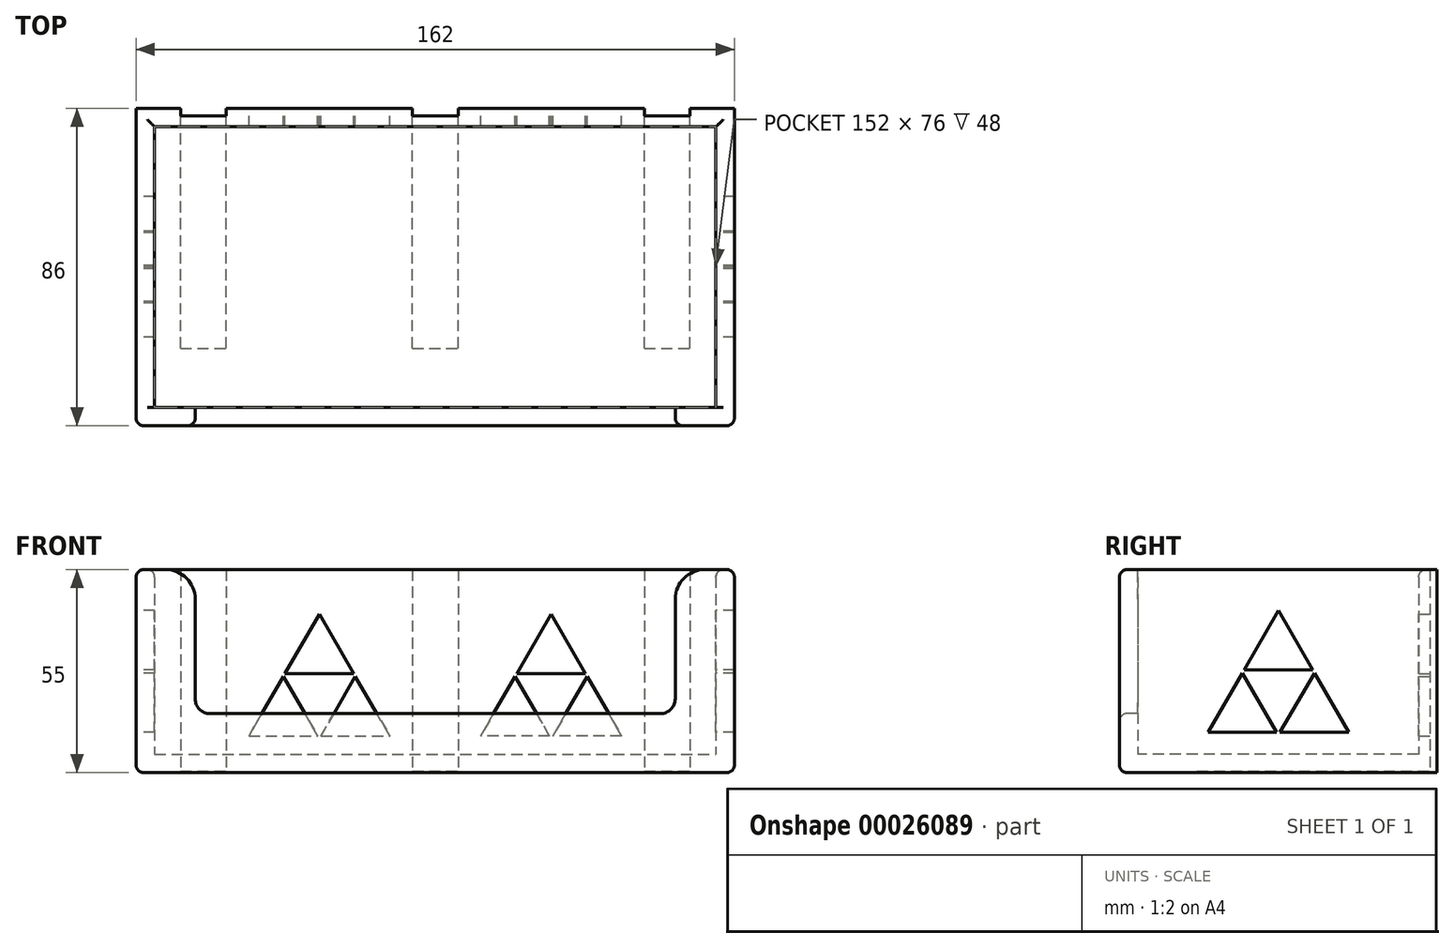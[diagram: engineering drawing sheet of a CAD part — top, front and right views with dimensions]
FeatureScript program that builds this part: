
annotation { "Feature Type Name" : "Feature", "Feature Type Description" : "" }
export const myFeature = defineFeature(function(context is Context, id is Id, definition is map)
    precondition{}
    {
        {
            var Q0;
            Q0=qCreatedBy(makeId("Top.planeOp"),FACE);
            var sketch = newSketch(context, id + "F0", { "sketchPlane" : qUnion([Q0])});
            skLineSegment(sketch, "E0.bottom", {"start": v(-78.63, 86.65) * mm, "end": v(73.37, 86.65) * mm});
            skLineSegment(sketch, "E0.top", {"start": v(-78.63, 10.65) * mm, "end": v(73.37, 10.65) * mm});
            skLineSegment(sketch, "E0.left", {"start": v(-78.63, 86.65) * mm, "end": v(-78.63, 10.65) * mm});
            skLineSegment(sketch, "E0.right", {"start": v(73.37, 86.65) * mm, "end": v(73.37, 10.65) * mm});
            skSolve(sketch);
        }
        {
            var Q0;
            Q0=makeQuery(id+"F0.imprint","IMPRINT",FACE,{"disambiguationData":[TD([[makeQuery(id+"F0.imprint","IMPRINT",EDGE,{"derivedFrom":sQuery(id+"F0.wireOp",EDGE,"E0.bottom")}),-1.0]])]});
            extrude(context, id + "F1", {"entities" : qUnion([Q0]), "depth" : 5 * mm});
        }
        {
            var Q0;
            Q0=qCreatedBy(makeId("Top.planeOp"),FACE);
            var sketch = newSketch(context, id + "F2", { "sketchPlane" : qUnion([Q0])});
            skLineSegment(sketch, "E1.0", {"start": v(-78.63, 10.65) * mm, "end": v(73.37, 10.65) * mm});
            skLineSegment(sketch, "E2.0", {"start": v(-78.63, 86.65) * mm, "end": v(-78.63, 10.65) * mm});
            skLineSegment(sketch, "E3.0", {"start": v(-78.63, 86.65) * mm, "end": v(73.37, 86.65) * mm});
            skLineSegment(sketch, "E4.0", {"start": v(73.37, 86.65) * mm, "end": v(73.37, 10.65) * mm});
            skLineSegment(sketch, "E5.0", {"start": v(-83.63, 5.65) * mm, "end": v(78.37, 5.65) * mm});
            skLineSegment(sketch, "E6.0", {"start": v(-83.63, 91.65) * mm, "end": v(78.37, 91.65) * mm});
            skLineSegment(sketch, "E7.0", {"start": v(-83.63, 91.65) * mm, "end": v(-83.63, 5.65) * mm});
            skLineSegment(sketch, "E8.0", {"start": v(78.37, 91.65) * mm, "end": v(78.37, 5.65) * mm});
            skSolve(sketch);
        }
        {
            var Q0;
            Q0=makeQuery(id+"F2.imprint","IMPRINT",FACE,{"disambiguationData":[TD([[makeQuery(id+"F2.imprint","IMPRINT",EDGE,{"derivedFrom":sQuery(id+"F2.wireOp",EDGE,"E1.0")}),-1.0]])]});
            extrude(context, id + "F3", {"entities" : qUnion([Q0]), "operationType" : NewBodyOperationType.ADD, "depth" : 55 * mm});
        }
        {
            var Q0;
            Q0=makeQuery(id+"F3.opExtrude","SWEPT_FACE",FACE,{"disambiguationData":[OSD([sQuery(id+"F2.wireOp",EDGE,"E5.0")])]});
            var sketch = newSketch(context, id + "F4", { "sketchPlane" : qUnion([Q0])});
            skLineSegment(sketch, "E9.0", {"start": v(-63.63, 16) * mm, "end": v(58.37, 16) * mm});
            skLineSegment(sketch, "E10.0", {"start": v(-67.63, 47) * mm, "end": v(-67.63, 20) * mm});
            skLineSegment(sketch, "E11.0", {"start": v(62.37, 47) * mm, "end": v(62.37, 20) * mm});
            skLineSegment(sketch, "E12.0", {"start": v(-83.63, 55) * mm, "end": v(-75.63, 55) * mm});
            skLineSegment(sketch, "E13.trimOffspring", {"start": v(70.37, 55) * mm, "end": v(78.37, 55) * mm});
            skPoint(sketch, "E14.visualSharp", {"position": v(-67.63, 55) * mm});
            skArc(sketch, "E14.filletArc", {"start": v(-67.63, 47) * mm, "mid": v(-69.98, 52.66) * mm, "end": v(-75.63, 55) * mm});
            skPoint(sketch, "E15.visualSharp", {"position": v(62.37, 55) * mm});
            skArc(sketch, "E15.filletArc", {"start": v(70.37, 55) * mm, "mid": v(64.7, 52.66) * mm, "end": v(62.37, 47) * mm});
            skPoint(sketch, "E16.visualSharp", {"position": v(-67.63, 16) * mm});
            skArc(sketch, "E16.filletArc", {"start": v(-67.63, 20) * mm, "mid": v(-66.46, 17.17) * mm, "end": v(-63.63, 16) * mm});
            skPoint(sketch, "E17.visualSharp", {"position": v(62.37, 16) * mm});
            skArc(sketch, "E17.filletArc", {"start": v(58.37, 16) * mm, "mid": v(61.2, 17.17) * mm, "end": v(62.37, 20) * mm});
            skSolve(sketch);
        }
        {
            var Q0;
            Q0=makeQuery(id+"F4.imprint","IMPRINT",FACE,{"disambiguationData":[TD([[makeQuery(id+"F4.imprint","IMPRINT",EDGE,{"derivedFrom":sQuery(id+"F4.wireOp",EDGE,"E9.0")}),1.0]])]});
            var Q1;
            Q1=makeQuery(id+"F3.opExtrude","SWEPT_FACE",FACE,{"disambiguationData":[OSD([sQuery(id+"F2.wireOp",EDGE,"E1.0")])]});
            extrude(context, id + "F5", {"entities" : qUnion([Q0]), "operationType" : NewBodyOperationType.REMOVE, "endBound" : BoundingType.UP_TO_SURFACE, "oppositeDirection" : true, "endBoundEntityFace" : qUnion([Q1]), "depth" : 25.4 * mm});
        }
        {
            var Q0;
            Q0=makeQuery(id+"F3.opExtrude","SWEPT_FACE",FACE,{"disambiguationData":[OSD([sQuery(id+"F2.wireOp",EDGE,"E6.0")])]});
            var sketch = newSketch(context, id + "F6", { "sketchPlane" : qUnion([Q0])});
            skLineSegment(sketch, "E18.0", {"start": v(-78.37, 55) * mm, "end": v(-78.37, 0) * mm});
            skLineSegment(sketch, "E19.0", {"start": v(83.63, 0) * mm, "end": v(-78.37, 0) * mm});
            skLineSegment(sketch, "E20.0", {"start": v(83.63, 55) * mm, "end": v(83.63, 0) * mm});
            skLineSegment(sketch, "E21.0", {"start": v(83.63, 55) * mm, "end": v(-78.37, 55) * mm});
            skLineSegment(sketch, "E22", {"start": v(2.63, 55) * mm, "end": v(2.63, 0) * mm, "construction": true});
            skLineSegment(sketch, "E23.0", {"start": v(-3.57, 70) * mm, "end": v(-3.57, 0) * mm});
            skLineSegment(sketch, "E24.0", {"start": v(8.83, 70) * mm, "end": v(8.83, 0) * mm});
            skLineSegment(sketch, "E25.0", {"start": v(-66.37, 70) * mm, "end": v(-66.37, 0) * mm});
            skLineSegment(sketch, "E26.0", {"start": v(-53.97, 70) * mm, "end": v(-53.97, 0) * mm});
            skLineSegment(sketch, "E27.0", {"start": v(71.63, 70) * mm, "end": v(71.63, 0) * mm});
            skLineSegment(sketch, "E28.0", {"start": v(59.23, 70) * mm, "end": v(59.23, 0) * mm});
            skSolve(sketch);
        }
        {
            var Q0;
            {var subQ0=sQuery(id+"F6.wireOp",EDGE,"E25.0");Q0=makeQuery(id+"F6.imprint","IMPRINT",FACE,{"disambiguationData":[TD([[makeQuery(id+"F6.imprint","IMPRINT",EDGE,{"derivedFrom":subQ0}),1.0]])]});}
            var Q1;
            {var subQ0=sQuery(id+"F6.wireOp",EDGE,"E23.0");Q1=makeQuery(id+"F6.imprint","IMPRINT",FACE,{"disambiguationData":[TD([[makeQuery(id+"F6.imprint","IMPRINT",EDGE,{"derivedFrom":subQ0}),1.0]])]});}
            var Q2;
            {var subQ0=sQuery(id+"F6.wireOp",EDGE,"E27.0");Q2=makeQuery(id+"F6.imprint","IMPRINT",FACE,{"disambiguationData":[TD([[makeQuery(id+"F6.imprint","IMPRINT",EDGE,{"derivedFrom":subQ0}),-1.0]])]});}
            extrude(context, id + "F7", {"entities" : qUnion([Q0, Q1, Q2]), "operationType" : NewBodyOperationType.REMOVE, "oppositeDirection" : true, "depth" : 2 * mm});
        }
        {
            var Q0;
            Q0=makeQuery(id+"F3.boolean.opBoolean","MERGE",FACE,{"derivedFrom":[makeQuery(id+"F1.opExtrude","CAP_FACE",FACE,{"disambiguationData":[OSD([sQuery(id+"F0.wireOp",EDGE,"E0.bottom"),sQuery(id+"F0.wireOp",EDGE,"E0.top"),sQuery(id+"F0.wireOp",EDGE,"E0.left"),sQuery(id+"F0.wireOp",EDGE,"E0.right")])],"isStart":true}),makeQuery(id+"F3.opExtrude","CAP_FACE",FACE,{"disambiguationData":[OSD([sQuery(id+"F2.wireOp",EDGE,"E1.0"),sQuery(id+"F2.wireOp",EDGE,"E2.0"),sQuery(id+"F2.wireOp",EDGE,"E3.0"),sQuery(id+"F2.wireOp",EDGE,"E4.0"),sQuery(id+"F2.wireOp",EDGE,"E5.0"),sQuery(id+"F2.wireOp",EDGE,"E6.0"),sQuery(id+"F2.wireOp",EDGE,"E7.0"),sQuery(id+"F2.wireOp",EDGE,"E8.0")])],"isStart":true})]});
            var sketch = newSketch(context, id + "F8", { "sketchPlane" : qUnion([Q0])});
            skLineSegment(sketch, "E29.0", {"start": v(66.37, -91.65) * mm, "end": v(78.37, -91.65) * mm, "construction": true});
            skLineSegment(sketch, "E30.0", {"start": v(78.37, -91.65) * mm, "end": v(78.37, -5.65) * mm, "construction": true});
            skLineSegment(sketch, "E31.0", {"start": v(53.97, -89.65) * mm, "end": v(66.37, -89.65) * mm});
            skLineSegment(sketch, "E32.0", {"start": v(66.37, -26.65) * mm, "end": v(66.37, -91.65) * mm});
            skLineSegment(sketch, "E33.0", {"start": v(53.97, -26.65) * mm, "end": v(53.97, -91.65) * mm});
            skLineSegment(sketch, "E34.0", {"start": v(3.57, -91.65) * mm, "end": v(53.97, -91.65) * mm, "construction": true});
            skLineSegment(sketch, "E35.0", {"start": v(3.57, -26.65) * mm, "end": v(3.57, -91.65) * mm});
            skLineSegment(sketch, "E36.0", {"start": v(-8.83, -89.65) * mm, "end": v(3.57, -89.65) * mm});
            skLineSegment(sketch, "E37.0", {"start": v(-8.83, -26.65) * mm, "end": v(-8.83, -91.65) * mm});
            skLineSegment(sketch, "E38.0", {"start": v(-59.23, -91.65) * mm, "end": v(-8.83, -91.65) * mm, "construction": true});
            skLineSegment(sketch, "E39.0", {"start": v(-59.23, -26.65) * mm, "end": v(-59.23, -91.65) * mm});
            skLineSegment(sketch, "E40.0", {"start": v(-71.63, -89.65) * mm, "end": v(-59.23, -89.65) * mm});
            skLineSegment(sketch, "E41.0", {"start": v(-71.63, -26.65) * mm, "end": v(-71.63, -91.65) * mm});
            skLineSegment(sketch, "E42.0", {"start": v(-83.63, -91.65) * mm, "end": v(-71.63, -91.65) * mm, "construction": true});
            skLineSegment(sketch, "E43.0", {"start": v(-83.63, -91.65) * mm, "end": v(-83.63, -5.65) * mm, "construction": true});
            skLineSegment(sketch, "E44.0", {"start": v(-71.63, -26.65) * mm, "end": v(-59.23, -26.65) * mm});
            skLineSegment(sketch, "E45.trimOffspring", {"start": v(53.97, -26.65) * mm, "end": v(66.37, -26.65) * mm});
            skLineSegment(sketch, "E46.trimOffspring", {"start": v(-8.83, -26.65) * mm, "end": v(3.57, -26.65) * mm});
            skSolve(sketch);
        }
        {
            var Q0;
            {var subQ0=sQuery(id+"F8.wireOp",EDGE,"E36.0");Q0=makeQuery(id+"F8.imprint","IMPRINT",FACE,{"disambiguationData":[TD([[makeQuery(id+"F8.imprint","IMPRINT",EDGE,{"derivedFrom":subQ0}),1.0]])]});}
            var Q1;
            {var subQ0=sQuery(id+"F8.wireOp",EDGE,"E40.0");Q1=makeQuery(id+"F8.imprint","IMPRINT",FACE,{"disambiguationData":[TD([[makeQuery(id+"F8.imprint","IMPRINT",EDGE,{"derivedFrom":subQ0}),1.0]])]});}
            var Q2;
            {var subQ0=sQuery(id+"F8.wireOp",EDGE,"E31.0");Q2=makeQuery(id+"F8.imprint","IMPRINT",FACE,{"disambiguationData":[TD([[makeQuery(id+"F8.imprint","IMPRINT",EDGE,{"derivedFrom":subQ0}),1.0]])]});}
            extrude(context, id + "F9", {"entities" : qUnion([Q0, Q1, Q2]), "operationType" : NewBodyOperationType.REMOVE, "oppositeDirection" : true, "depth" : .4 * mm});
        }
        {
            var Q0;
            Q0=makeQuery(id+"F3.opExtrude","SWEPT_FACE",FACE,{"disambiguationData":[OSD([sQuery(id+"F2.wireOp",EDGE,"E7.0")])]});
            var sketch = newSketch(context, id + "F10", { "sketchPlane" : qUnion([Q0])});
            skLineSegment(sketch, "E47.0", {"start": v(-91.65, 55) * mm, "end": v(-5.65, 55) * mm});
            skLineSegment(sketch, "E48.0", {"start": v(-91.65, 55) * mm, "end": v(-91.65, 0) * mm});
            skLineSegment(sketch, "E49.0", {"start": v(-91.65, 0) * mm, "end": v(-5.65, 0) * mm});
            skLineSegment(sketch, "E50.0", {"start": v(-5.65, 55) * mm, "end": v(-5.65, 0) * mm});
            skLineSegment(sketch, "E51.2", {"start": v(-67.7, 10.9) * mm, "end": v(-49.11, 10.9) * mm});
            skLineSegment(sketch, "E52", {"start": v(-48.65, 43.9) * mm, "end": v(-57.95, 27.8) * mm});
            skLineSegment(sketch, "E53", {"start": v(-48.65, 43.9) * mm, "end": v(-39.36, 27.8) * mm});
            skPoint(sketch, "E51.1.start.orphan", {"position": v(-80.85, 43.9) * mm});
            skPoint(sketch, "E54.orphan", {"position": v(-80.85, 10.9) * mm});
            skPoint(sketch, "E51.3.end.orphan", {"position": v(-16.45, 10.9) * mm});
            skPoint(sketch, "E51.0.end.orphan", {"position": v(-16.45, 43.9) * mm});
            skLineSegment(sketch, "E55.0", {"start": v(-57.95, 27.8) * mm, "end": v(-39.36, 27.8) * mm});
            skLineSegment(sketch, "E55.1", {"start": v(-49.11, 10.9) * mm, "end": v(-58.41, 27) * mm});
            skLineSegment(sketch, "E55.2", {"start": v(-38.9, 27) * mm, "end": v(-48.2, 10.9) * mm});
            skPoint(sketch, "E56.start.orphan", {"position": v(-39.13, 27.4) * mm});
            skPoint(sketch, "E57.end.orphan", {"position": v(-58.18, 27.4) * mm});
            skPoint(sketch, "E57.start.orphan", {"position": v(-48.65, 10.9) * mm});
            skLineSegment(sketch, "E58.trimOffspring", {"start": v(-38.9, 27) * mm, "end": v(-29.6, 10.9) * mm});
            skLineSegment(sketch, "E59.trimOffspring", {"start": v(-48.2, 10.9) * mm, "end": v(-29.6, 10.9) * mm});
            skLineSegment(sketch, "E60.trimOffspring", {"start": v(-58.41, 27) * mm, "end": v(-67.7, 10.9) * mm});
            skLineSegment(sketch, "E61", {"start": v(-48.65, 43.9) * mm, "end": v(-48.65, 55) * mm, "construction": true});
            skLineSegment(sketch, "E62", {"start": v(-48.65, 10.9) * mm, "end": v(-48.65, 0) * mm, "construction": true});
            skSolve(sketch);
        }
        {
            var Q0;
            Q0=makeQuery(id+"F10.imprint","IMPRINT",FACE,{"disambiguationData":[TD([[makeQuery(id+"F10.imprint","IMPRINT",EDGE,{"derivedFrom":sQuery(id+"F10.wireOp",EDGE,"E52")}),1.0]])]});
            var Q1;
            Q1=makeQuery(id+"F10.imprint","IMPRINT",FACE,{"disambiguationData":[TD([[makeQuery(id+"F10.imprint","IMPRINT",EDGE,{"derivedFrom":sQuery(id+"F10.wireOp",EDGE,"E51.2")}),1.0]])]});
            var Q2;
            Q2=makeQuery(id+"F10.imprint","IMPRINT",FACE,{"disambiguationData":[TD([[makeQuery(id+"F10.imprint","IMPRINT",EDGE,{"derivedFrom":sQuery(id+"F10.wireOp",EDGE,"E55.2")}),1.0]])]});
            extrude(context, id + "F11", {"entities" : qUnion([Q0, Q1, Q2]), "operationType" : NewBodyOperationType.REMOVE, "endBound" : BoundingType.THROUGH_ALL, "oppositeDirection" : true, "depth" : 25.4 * mm});
        }
        {
            var Q0;
            {var subQ2=sQuery(id+"F2.wireOp",EDGE,"E6.0");Q0=makeQuery(id+"F7.boolean.opBoolean","SPLIT",FACE,{"disambiguationData":[TD([makeQuery(id+"F7.opExtrude","SWEPT_FACE",FACE,{"disambiguationData":[OSD([sQuery(id+"F6.wireOp",EDGE,"E24.0")])]})])],"derivedFrom":makeQuery(id+"F3.opExtrude","SWEPT_FACE",FACE,{"disambiguationData":[OSD([subQ2])]})});}
            var Q1;
            {var subQ2=sQuery(id+"F2.wireOp",EDGE,"E6.0");Q1=makeQuery(id+"F7.boolean.opBoolean","SPLIT",FACE,{"disambiguationData":[TD([makeQuery(id+"F7.opExtrude","SWEPT_FACE",FACE,{"disambiguationData":[OSD([sQuery(id+"F6.wireOp",EDGE,"E24.0")])]})])],"derivedFrom":makeQuery(id+"F3.opExtrude","SWEPT_FACE",FACE,{"disambiguationData":[OSD([subQ2])]})});}
            var sketch = newSketch(context, id + "F12", { "sketchPlane" : qUnion([Q0, Q1])});
            skLineSegment(sketch, "E63.0", {"start": v(59.23, 55) * mm, "end": v(8.83, 55) * mm, "construction": true});
            skLineSegment(sketch, "E64.0", {"start": v(8.83, 55) * mm, "end": v(8.83, 0) * mm, "construction": true});
            skLineSegment(sketch, "E65.0", {"start": v(59.23, 0) * mm, "end": v(8.83, 0) * mm, "construction": true});
            skLineSegment(sketch, "E66.0", {"start": v(59.23, 55) * mm, "end": v(59.23, 0) * mm, "construction": true});
            skLineSegment(sketch, "E67.0", {"start": v(78.63, 55) * mm, "end": v(-73.37, 55) * mm, "construction": true});
            skLineSegment(sketch, "E68.2", {"start": v(53.09, 9.98) * mm, "end": v(34.5, 9.98) * mm});
            skLineSegment(sketch, "E69", {"start": v(34.03, 42.98) * mm, "end": v(24.74, 26.88) * mm});
            skLineSegment(sketch, "E70", {"start": v(34.03, 42.98) * mm, "end": v(43.33, 26.88) * mm});
            skPoint(sketch, "E68.3.start.orphan", {"position": v(16.15, 31.6) * mm});
            skPoint(sketch, "E68.0.start.orphan", {"position": v(51.92, 54.36) * mm});
            skPoint(sketch, "E71.orphan", {"position": v(55.23, 9.98) * mm});
            skPoint(sketch, "E72.orphan", {"position": v(12.83, 9.98) * mm});
            skLineSegment(sketch, "E73.0", {"start": v(24.74, 26.88) * mm, "end": v(43.33, 26.88) * mm});
            skLineSegment(sketch, "E73.1", {"start": v(33.57, 9.98) * mm, "end": v(24.28, 26.08) * mm});
            skLineSegment(sketch, "E73.2", {"start": v(43.8, 26.08) * mm, "end": v(34.5, 9.98) * mm});
            skLineSegment(sketch, "E74.trimOffspring", {"start": v(24.28, 26.08) * mm, "end": v(14.98, 9.98) * mm});
            skLineSegment(sketch, "E75.trimOffspring", {"start": v(33.57, 9.98) * mm, "end": v(14.98, 9.98) * mm});
            skLineSegment(sketch, "E76.trimOffspring", {"start": v(43.8, 26.08) * mm, "end": v(53.09, 9.98) * mm});
            skPoint(sketch, "E77.start.orphan", {"position": v(43.56, 26.48) * mm});
            skPoint(sketch, "E78.end.orphan", {"position": v(24.5, 26.48) * mm});
            skPoint(sketch, "E78.start.orphan", {"position": v(34.03, 9.98) * mm});
            skLineSegment(sketch, "E79", {"start": v(2.63, 55) * mm, "end": v(2.63, 0) * mm, "construction": true});
            skLineSegment(sketch, "E80.MirrorCS", {"start": v(-28.77, 42.98) * mm, "end": v(-19.47, 26.88) * mm});
            skLineSegment(sketch, "E81.MirrorCS", {"start": v(-28.77, 42.98) * mm, "end": v(-38.06, 26.88) * mm});
            skLineSegment(sketch, "E82.MirrorCS", {"start": v(-19.47, 26.88) * mm, "end": v(-38.06, 26.88) * mm});
            skLineSegment(sketch, "E83.MirrorCS", {"start": v(-19, 26.08) * mm, "end": v(-9.71, 9.98) * mm});
            skLineSegment(sketch, "E84.MirrorCS", {"start": v(-28.3, 9.98) * mm, "end": v(-19, 26.08) * mm});
            skLineSegment(sketch, "E85.MirrorCS", {"start": v(-28.3, 9.98) * mm, "end": v(-9.71, 9.98) * mm});
            skLineSegment(sketch, "E86.MirrorCS", {"start": v(-38.52, 26.08) * mm, "end": v(-29.23, 9.98) * mm});
            skLineSegment(sketch, "E87.MirrorCS", {"start": v(-47.82, 9.98) * mm, "end": v(-29.23, 9.98) * mm});
            skLineSegment(sketch, "E88.MirrorCS", {"start": v(-38.52, 26.08) * mm, "end": v(-47.82, 9.98) * mm});
            skLineSegment(sketch, "E89", {"start": v(34.03, 42.98) * mm, "end": v(34.03, 55) * mm, "construction": true});
            skLineSegment(sketch, "E90", {"start": v(34.03, 9.98) * mm, "end": v(34.03, 0) * mm, "construction": true});
            skSolve(sketch);
        }
        {
            var Q0;
            Q0=makeQuery(id+"F12.imprint","IMPRINT",FACE,{"disambiguationData":[TD([[makeQuery(id+"F12.imprint","IMPRINT",EDGE,{"derivedFrom":sQuery(id+"F12.wireOp",EDGE,"E80.MirrorCS")}),-1.0]])]});
            var Q1;
            Q1=makeQuery(id+"F12.imprint","IMPRINT",FACE,{"disambiguationData":[TD([[makeQuery(id+"F12.imprint","IMPRINT",EDGE,{"derivedFrom":sQuery(id+"F12.wireOp",EDGE,"E86.MirrorCS")}),-1.0]])]});
            var Q2;
            Q2=makeQuery(id+"F12.imprint","IMPRINT",FACE,{"disambiguationData":[TD([[makeQuery(id+"F12.imprint","IMPRINT",EDGE,{"derivedFrom":sQuery(id+"F12.wireOp",EDGE,"E83.MirrorCS")}),-1.0]])]});
            var Q3;
            Q3=makeQuery(id+"F12.imprint","IMPRINT",FACE,{"disambiguationData":[TD([[makeQuery(id+"F12.imprint","IMPRINT",EDGE,{"derivedFrom":sQuery(id+"F12.wireOp",EDGE,"E73.1")}),1.0]])]});
            var Q4;
            Q4=makeQuery(id+"F12.imprint","IMPRINT",FACE,{"disambiguationData":[TD([[makeQuery(id+"F12.imprint","IMPRINT",EDGE,{"derivedFrom":sQuery(id+"F12.wireOp",EDGE,"E69")}),1.0]])]});
            var Q5;
            Q5=makeQuery(id+"F12.imprint","IMPRINT",FACE,{"disambiguationData":[TD([[makeQuery(id+"F12.imprint","IMPRINT",EDGE,{"derivedFrom":sQuery(id+"F12.wireOp",EDGE,"E68.2")}),-1.0]])]});
            extrude(context, id + "F13", {"entities" : qUnion([Q0, Q1, Q2, Q3, Q4, Q5]), "operationType" : NewBodyOperationType.REMOVE, "endBound" : BoundingType.UP_TO_NEXT, "oppositeDirection" : true, "depth" : 25.4 * mm});
        }
        {
            var Q0;
            Q0=makeQuery(id+"F3.opExtrude","SWEPT_EDGE",EDGE,{"disambiguationData":[OSD([sQuery(id+"F2.wireOp",EDGE,"E5.0"),sQuery(id+"F2.wireOp",EDGE,"E7.0")])]});
            var Q1;
            {var subQ0=sQuery(id+"F2.wireOp",EDGE,"E7.0");var subQ1=sQuery(id+"F2.wireOp",EDGE,"E5.0");Q1=makeQuery(id+"F5.boolean.opBoolean","SPLIT",EDGE,{"disambiguationData":[TD([makeQuery(id+"F3.opExtrude","SWEPT_FACE",FACE,{"disambiguationData":[OSD([subQ0])]})])],"derivedFrom":makeQuery(id+"F3.opExtrude","CAP_EDGE",EDGE,{"disambiguationData":[OSD([subQ1])],"isStart":false})});}
            var Q2;
            Q2=makeQuery(id+"F5.boolean.opBoolean","COPY",EDGE,{"derivedFrom":makeQuery(id+"F5.opExtrude","CAP_EDGE",EDGE,{"disambiguationData":[OSD([sQuery(id+"F4.wireOp",EDGE,"E9.0")])],"isStart":true})});
            var Q3;
            Q3=makeQuery(id+"F5.boolean.opBoolean","COPY",EDGE,{"derivedFrom":makeQuery(id+"F5.opExtrude","CAP_EDGE",EDGE,{"disambiguationData":[OSD([sQuery(id+"F4.wireOp",EDGE,"E11.0")])],"isStart":true})});
            var Q4;
            Q4=makeQuery(id+"F5.boolean.opBoolean","COPY",EDGE,{"derivedFrom":makeQuery(id+"F5.opExtrude","CAP_EDGE",EDGE,{"disambiguationData":[OSD([sQuery(id+"F4.wireOp",EDGE,"E14.filletArc")])],"isStart":false})});
            var Q5;
            Q5=makeQuery(id+"F5.boolean.opBoolean","COPY",EDGE,{"derivedFrom":makeQuery(id+"F5.opExtrude","CAP_EDGE",EDGE,{"disambiguationData":[OSD([sQuery(id+"F4.wireOp",EDGE,"E9.0")])],"isStart":false})});
            var Q6;
            Q6=makeQuery(id+"F3.opExtrude","CAP_EDGE",EDGE,{"disambiguationData":[OSD([sQuery(id+"F2.wireOp",EDGE,"E5.0")])],"isStart":true});
            var Q7;
            Q7=makeQuery(id+"F3.opExtrude","SWEPT_EDGE",EDGE,{"disambiguationData":[OSD([sQuery(id+"F2.wireOp",EDGE,"E5.0"),sQuery(id+"F2.wireOp",EDGE,"E8.0")])]});
            var Q8;
            Q8=makeQuery(id+"F3.opExtrude","CAP_EDGE",EDGE,{"disambiguationData":[OSD([sQuery(id+"F2.wireOp",EDGE,"E8.0")])],"isStart":false});
            var Q9;
            Q9=makeQuery(id+"F3.opExtrude","CAP_EDGE",EDGE,{"disambiguationData":[OSD([sQuery(id+"F2.wireOp",EDGE,"E7.0")])],"isStart":false});
            var Q10;
            Q10=makeQuery(id+"F3.opExtrude","CAP_EDGE",EDGE,{"disambiguationData":[OSD([sQuery(id+"F2.wireOp",EDGE,"E7.0")])],"isStart":true});
            var Q11;
            Q11=makeQuery(id+"F3.opExtrude","CAP_EDGE",EDGE,{"disambiguationData":[OSD([sQuery(id+"F2.wireOp",EDGE,"E8.0")])],"isStart":true});
            var Q12;
            Q12=makeQuery(id+"F9.boolean.opBoolean","COPY",EDGE,{"derivedFrom":makeQuery(id+"F9.opExtrude","CAP_EDGE",EDGE,{"disambiguationData":[OSD([sQuery(id+"F8.wireOp",EDGE,"E31.0")])],"isStart":false})});
            var Q13;
            Q13=makeQuery(id+"F9.boolean.opBoolean","COPY",EDGE,{"derivedFrom":makeQuery(id+"F9.opExtrude","CAP_EDGE",EDGE,{"disambiguationData":[OSD([sQuery(id+"F8.wireOp",EDGE,"E36.0")])],"isStart":false})});
            var Q14;
            Q14=makeQuery(id+"F9.boolean.opBoolean","COPY",EDGE,{"derivedFrom":makeQuery(id+"F9.opExtrude","CAP_EDGE",EDGE,{"disambiguationData":[OSD([sQuery(id+"F8.wireOp",EDGE,"E40.0")])],"isStart":false})});
            var Q15;
            Q15=makeQuery(id+"F3.opExtrude","CAP_EDGE",EDGE,{"disambiguationData":[OSD([sQuery(id+"F2.wireOp",EDGE,"E2.0")])],"isStart":false});
            var Q16;
            Q16=makeQuery(id+"F3.opExtrude","CAP_EDGE",EDGE,{"disambiguationData":[OSD([sQuery(id+"F2.wireOp",EDGE,"E3.0")])],"isStart":false});
            var Q17;
            Q17=makeQuery(id+"F3.opExtrude","CAP_EDGE",EDGE,{"disambiguationData":[OSD([sQuery(id+"F2.wireOp",EDGE,"E4.0")])],"isStart":false});
            fillet(context, id + "F14", {"entities" : qUnion([Q0, Q1, Q2, Q3, Q4, Q5, Q6, Q7, Q8, Q9, Q10, Q11, Q12, Q13, Q14, Q15, Q16, Q17]), "radius" : 2 * mm, "tangentPropagation" : true, "allowEdgeOverflow" : false});
        }
    });
